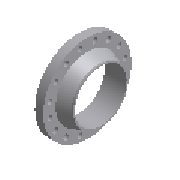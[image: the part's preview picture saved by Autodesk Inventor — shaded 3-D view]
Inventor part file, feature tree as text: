
AUTODESK INVENTOR PART (.ipt)
format: ipt  version: 2017.3 (Build 213257000, 257)  size: 278,528 bytes
history: native  units: mm (DEFAULTED — no unit token found)
features: other x4, sketch x3, revolve x2, chamfer x2, extrude x1, pattern_circular x1, fillet x1
ambient origin geometry x8: Origin, YZ Plane, XZ Plane, XY Plane, X Axis, Y Axis, Z Axis, Center Point
bodies: Body1 (feature_tree)
feature tree (14):
  revolve  "Revolution1"  [1 undecoded]
  extrude  "Extrusion1"  Depth=1.524mm
  pattern_circular  "Circular Pattern1"  [2 undecoded]
  other  "Work Axis1"
  other  "Work Point1"
  other  "Work Axis2"
  other  "Work Point2"
  chamfer  "Chamfer1"  Angle=90.0deg  [1 undecoded]
  revolve  "Revolution2"  [1 undecoded]
  fillet  "Fillet1"  Radius=31.75mm
  chamfer  "Chamfer2"  Distance=25.4mm
  sketch  "Sketch1"  dims[d0=520.7mm d1=381.0mm]
  sketch  "Sketch2"  dims[d2=1.524mm d3=320.675mm]
  sketch  "Sketch3"  dims[d4=323.85mm d7=374.65mm d9=90.0deg d10=225.425mm d11=31.75mm d12=25.4mm d13=0.0mm d14=160.0mm d16=360.0deg d17=1.963495mm d18=49.276mm d20=128.524mm d21=14.280444mm d22=1.5875mm d23=3.175mm d24=45.0deg d25=25.4mm d26=330.2mm d27=355.6mm d28=1.5875mm d29=6.544985mm d30=12.7mm d31=82.55mm d32=11.1125mm d33=2.585579mm d34=90.0deg d35=0.79375mm d36=0.79375mm d37=3.175mm d38=45.0deg]
note: 5 required parameter values undecoded (feature->parameter linkage not recoverable at this tier; creation-order binding heuristic only, values carry confidence <= 0.55)